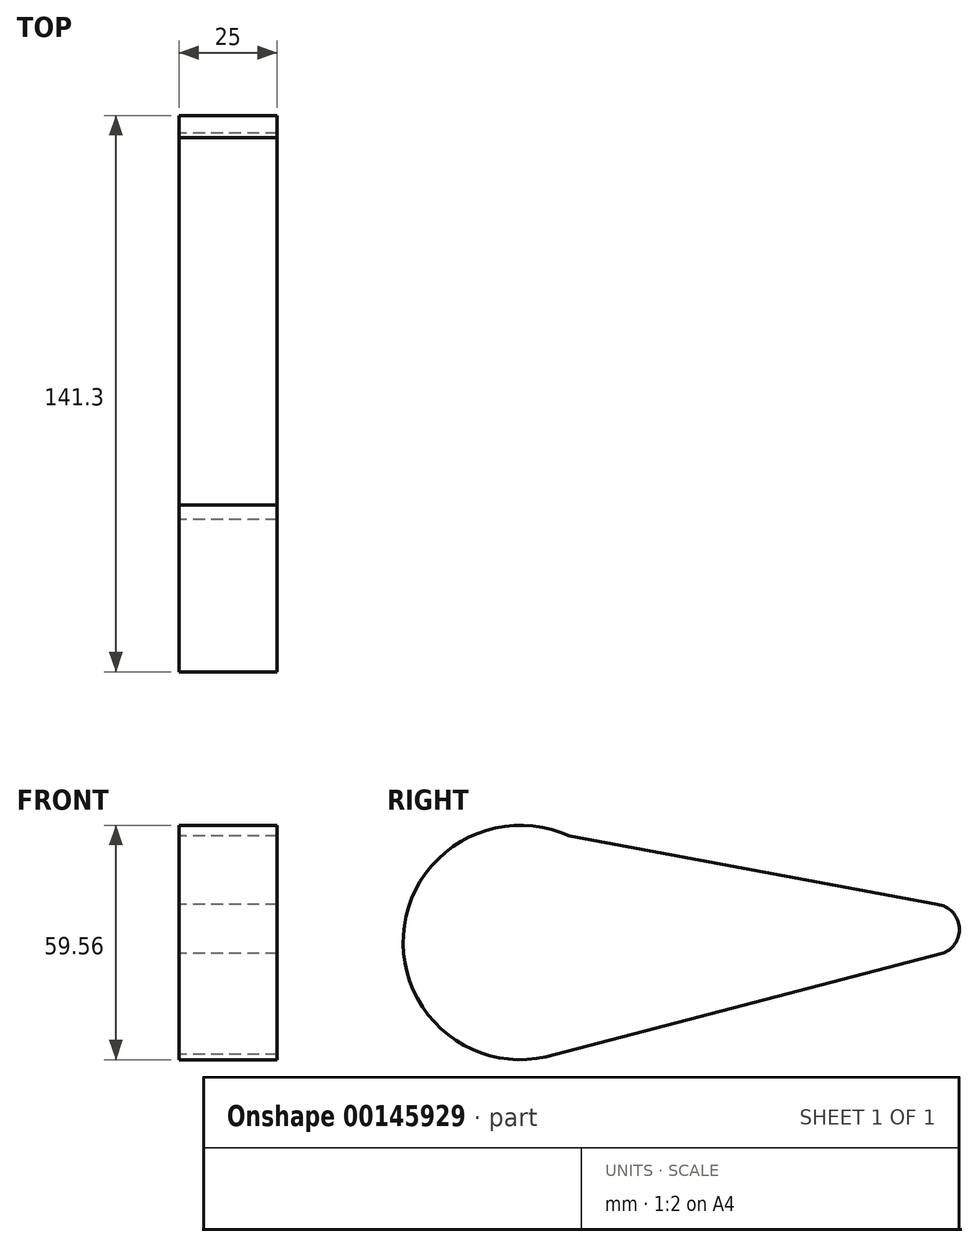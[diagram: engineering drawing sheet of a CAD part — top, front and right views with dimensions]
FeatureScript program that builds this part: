
annotation { "Feature Type Name" : "Feature", "Feature Type Description" : "" }
export const myFeature = defineFeature(function(context is Context, id is Id, definition is map)
    precondition{}
    {
        {
            var Q0;
            Q0=qCreatedBy(makeId("Right.planeOp"),FACE);
            var sketch = newSketch(context, id + "F0", { "sketchPlane" : qUnion([Q0])});
            skCircle(sketch, "E0", {"center": v(-3.1, -3.29) * mm, "radius": 29.78 * mm});
            skCircle(sketch, "E1", {"center": v(102, 0) * mm, "radius": 6.42 * mm});
            skLineSegment(sketch, "E2", {"start": v(9.43, 23.73) * mm, "end": v(102.84, 6.37) * mm});
            skLineSegment(sketch, "E3", {"start": v(5.81, -31.7) * mm, "end": v(103.93, -6.12) * mm});
            skSolve(sketch);
        }
        {
            var Q0;
            {var subQ0=sQuery(id+"F0.wireOp",EDGE,"E0");var subQ1=makeQuery(id+"F0.imprint","INTERSECT",VERTEX,{"derivedFrom":[subQ0,sQuery(id+"F0.wireOp",EDGE,"E2")]});Q0=makeQuery(id+"F0.imprint","IMPRINT",FACE,{"disambiguationData":[TD([[makeQuery(id+"F0.imprint","IMPRINT",EDGE,{"disambiguationData":[TD([[subQ1,-1.0]])],"derivedFrom":subQ0}),1.0]])]});}
            var Q1;
            {var subQ0=sQuery(id+"F0.wireOp",EDGE,"E2");Q1=makeQuery(id+"F0.imprint","IMPRINT",FACE,{"disambiguationData":[TD([[makeQuery(id+"F0.imprint","IMPRINT",EDGE,{"derivedFrom":subQ0}),-1.0]])]});}
            var Q2;
            {var subQ0=sQuery(id+"F0.wireOp",EDGE,"E1");var subQ1=makeQuery(id+"F0.imprint","INTERSECT",VERTEX,{"derivedFrom":[subQ0,sQuery(id+"F0.wireOp",EDGE,"E2")]});Q2=makeQuery(id+"F0.imprint","IMPRINT",FACE,{"disambiguationData":[TD([[makeQuery(id+"F0.imprint","IMPRINT",EDGE,{"disambiguationData":[TD([[subQ1,-1.0]])],"derivedFrom":subQ0}),1.0]])]});}
            extrude(context, id + "F1", {"entities" : qUnion([Q0, Q1, Q2]), "depth" : 25 * mm});
        }
    });
